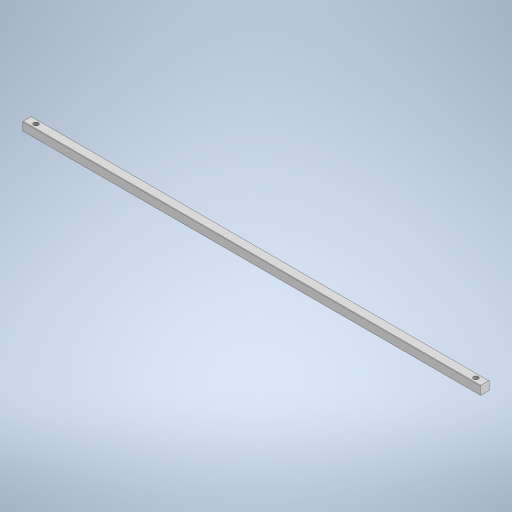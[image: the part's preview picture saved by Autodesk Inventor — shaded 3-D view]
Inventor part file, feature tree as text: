
AUTODESK INVENTOR PART (.ipt)
format: ipt  version: 2024.2 (Build 282272000, 272)  size: 266,752 bytes
history: native  units: in
note: dims shown in document units (in); Inventor stores cm internally (conversion verified against a paired STEP export)
features: extrude x2, thread x2, sketch x2, fillet x1
ambient origin geometry x8: Origin, YZ Plane, XZ Plane, XY Plane, X Axis, Y Axis, Z Axis, Center Point
bodies: Solid1 (feature_tree)
feature tree (7):
  extrude  "Extrusion1"  Depth=0.25in
  fillet  "Fillet1"  Radius=13.0in
  extrude  "Extrusion2"  Depth=0.25in
  thread  "Thread1"  [1 undecoded]
  thread  "Thread2"  [1 undecoded]
  sketch  "Sketch1"  dims[d0=0.25in d1=0.25in d2=13.0in d3=0.0in]
  sketch  "Sketch2"  dims[d4=0.0125in d5=0.1406in d6=0.25in d7=0.1406in d8=0.25in d9=0.25in d10=0.0in d11=0.25in d12=0.0in d13=0.25in d14=0.0in]
note: 2 required parameter values undecoded (feature->parameter linkage not recoverable at this tier; creation-order binding heuristic only, values carry confidence <= 0.55)
